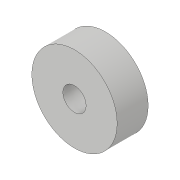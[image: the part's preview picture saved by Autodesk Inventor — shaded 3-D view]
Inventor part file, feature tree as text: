
AUTODESK INVENTOR PART (.ipt)
format: ipt  version: 2018.3 (Build 223284000, 284)  size: 81,408 bytes
history: native  units: in
note: dims shown in document units (in); Inventor stores cm internally (conversion verified against a paired STEP export)
features: extrude x1, sketch x1
ambient origin geometry x8: Origin, YZ Plane, XZ Plane, XY Plane, X Axis, Y Axis, Z Axis, Center Point
bodies: Solid1 (feature_tree)
feature tree (2):
  extrude  "Extrusion1"  Depth=0.25in
  sketch  "Sketch1"  dims[d0=0.1875in d1=0.6875in d2=0.25in d3=0.0in]
